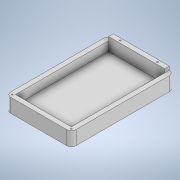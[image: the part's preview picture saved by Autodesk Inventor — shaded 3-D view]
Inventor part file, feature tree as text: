
AUTODESK INVENTOR PART (.ipt)
format: ipt  version: 2020 (Build 240168000, 168)  size: 1,729,536 bytes
history: native  units: mm
features: sketch x6, extrude x3, hole x2, emboss x2, fillet x1
ambient origin geometry x8: Origin, YZ Plane, XZ Plane, XY Plane, X Axis, Y Axis, Z Axis, Center Point
bodies: Solid1 (feature_tree)
feature tree (14):
  sketch  "Sketch1"  dims[d0=70.0mm d1=110.0mm]
  extrude  "Extrusion1"  Depth=110.0mm
  extrude  "Extrusion2"  Depth=100.0mm
  fillet  "Fillet1"  Radius=15.0mm
  extrude  "Extrusion3"  Depth=5.0mm
  hole  "Hole1"  [1 undecoded]
  hole  "Hole2"  [1 undecoded]
  emboss  "Emboss1"
  emboss  "Emboss2"
  sketch  "Sketch2"  dims[d2=60.0mm d3=100.0mm d4=15.0mm d5=0.0mm]
  sketch  "Sketch3"  dims[d6=5.0mm d7=0.0mm d8=5.0mm]
  sketch  "Sketch4"  dims[d9=60.0mm d10=4.0mm]
  sketch  "Sketch5"  dims[d11=5.0mm d12=0.0mm d13=2.5mm]
  sketch  "Sketch7"  dims[d14=135.0deg d15=2.5mm d16=1.5mm d17=6.0mm d18=2.5mm d19=1.0mm d20=14.3117mm d21=40.0mm d22=20.594885mm d23=20.0mm d24=0.0mm d25=20.0mm d26=180.0deg d27=1.5mm d28=6.0mm d29=2.5mm d30=1.0mm d31=14.3117mm d32=40.0mm d33=20.594885mm d34=1.0mm d35=0.0mm d46=0.5mm d47=0.0mm]
note: 2 required parameter values undecoded (feature->parameter linkage not recoverable at this tier; creation-order binding heuristic only, values carry confidence <= 0.55)
